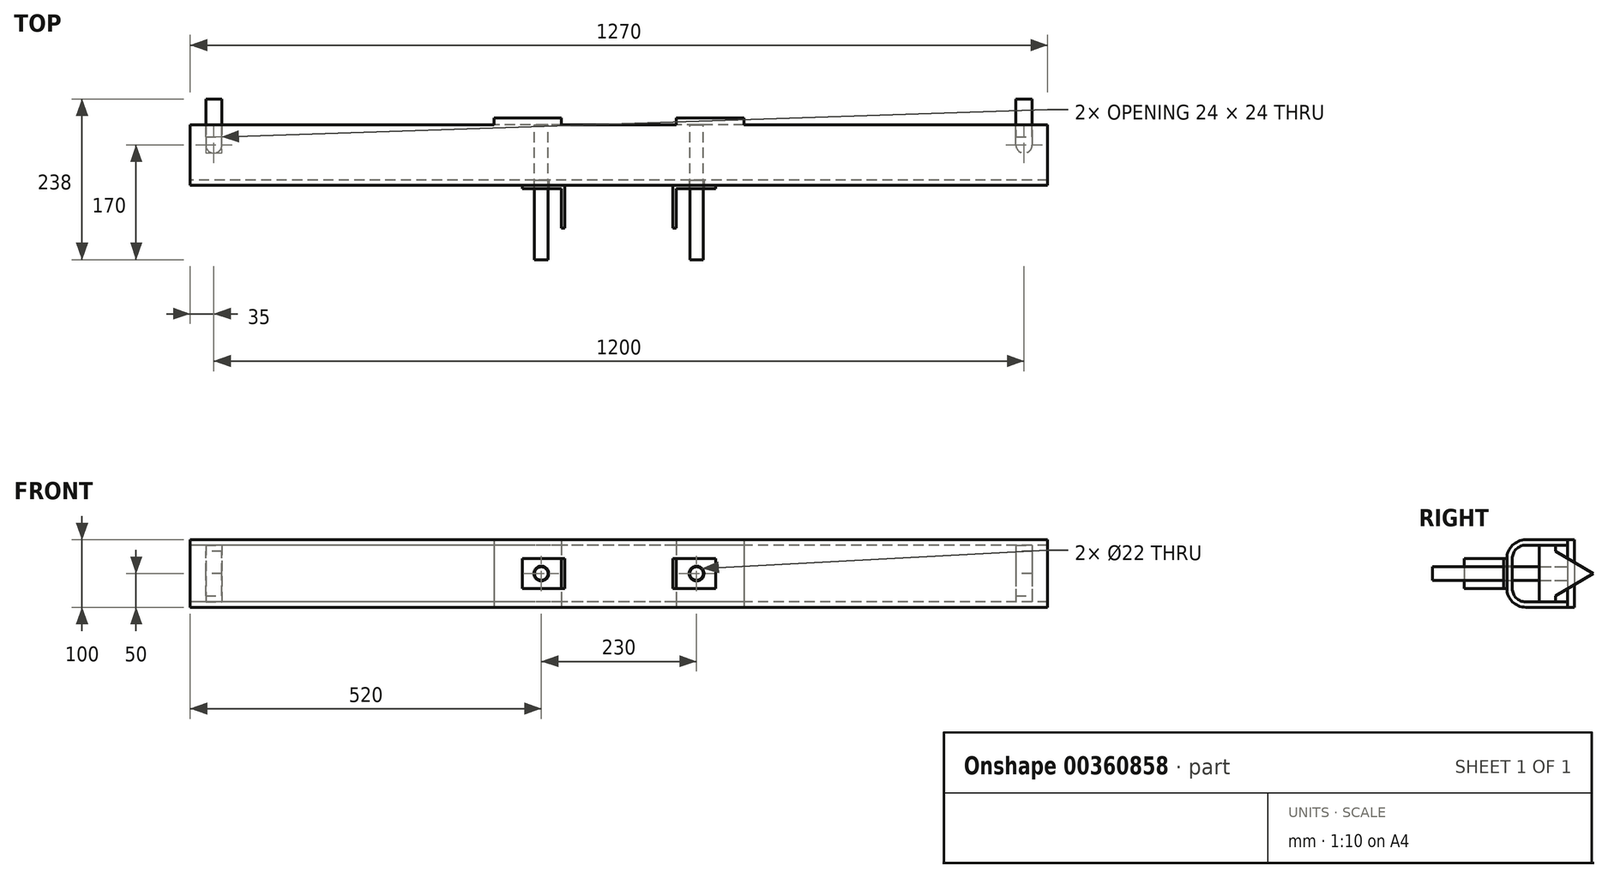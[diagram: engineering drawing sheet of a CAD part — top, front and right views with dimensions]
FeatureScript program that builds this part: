
annotation { "Feature Type Name" : "Feature", "Feature Type Description" : "" }
export const myFeature = defineFeature(function(context is Context, id is Id, definition is map)
    precondition{}
    {
        {
            var Q0;
            Q0=qCreatedBy(makeId("Right.planeOp"),FACE);
            var sketch = newSketch(context, id + "F0", { "sketchPlane" : qUnion([Q0])});
            skLineSegment(sketch, "E0", {"start": v(90, 50) * mm, "end": v(28, 50) * mm});
            skLineSegment(sketch, "E1", {"start": v(0, 22) * mm, "end": v(0, -22) * mm});
            skLineSegment(sketch, "E2", {"start": v(28, -50) * mm, "end": v(90, -50) * mm});
            skLineSegment(sketch, "E3", {"start": v(90, -50) * mm, "end": v(90, -42) * mm});
            skLineSegment(sketch, "E4", {"start": v(90, -42) * mm, "end": v(28, -42) * mm});
            skLineSegment(sketch, "E5", {"start": v(8, -22) * mm, "end": v(8, 22) * mm});
            skLineSegment(sketch, "E6", {"start": v(28, 42) * mm, "end": v(90, 42) * mm});
            skLineSegment(sketch, "E7", {"start": v(90, 42) * mm, "end": v(90, 50) * mm});
            skPoint(sketch, "E8.visualSharp", {"position": v(8, 42) * mm});
            skArc(sketch, "E8.filletArc", {"start": v(28, 42) * mm, "mid": v(13.86, 36.14) * mm, "end": v(8, 22) * mm});
            skPoint(sketch, "E9.visualSharp", {"position": v(8, -42) * mm});
            skArc(sketch, "E9.filletArc", {"start": v(8, -22) * mm, "mid": v(13.86, -36.14) * mm, "end": v(28, -42) * mm});
            skPoint(sketch, "E10.visualSharp", {"position": v(0, 50) * mm});
            skArc(sketch, "E10.filletArc", {"start": v(28, 50) * mm, "mid": v(8.2, 41.8) * mm, "end": v(0, 22) * mm});
            skPoint(sketch, "E11.visualSharp", {"position": v(0, -50) * mm});
            skArc(sketch, "E11.filletArc", {"start": v(0, -22) * mm, "mid": v(8.2, -41.8) * mm, "end": v(28, -50) * mm});
            skSolve(sketch);
        }
        {
            var Q0;
            Q0=qSketchRegion(id+"F0",true);
            extrude(context, id + "F1", {"entities" : qUnion([Q0]), "endBound" : BoundingType.SYMMETRIC, "depth" : 1270 * mm});
        }
        {
            var Q0;
            Q0=qCreatedBy(makeId("Top.planeOp"),FACE);
            var sketch = newSketch(context, id + "F2", { "sketchPlane" : qUnion([Q0])});
            skLineSegment(sketch, "E12", {"start": v(-143, 0) * mm, "end": v(-80, 0) * mm});
            skLineSegment(sketch, "E13", {"start": v(-80, 0) * mm, "end": v(-80, -63) * mm});
            skLineSegment(sketch, "E14.0", {"start": v(-85, -5) * mm, "end": v(-85, -63) * mm});
            skLineSegment(sketch, "E14.1", {"start": v(-143, -5) * mm, "end": v(-85, -5) * mm});
            skLineSegment(sketch, "E15", {"start": v(-143, -5) * mm, "end": v(-143, 0) * mm});
            skLineSegment(sketch, "E16", {"start": v(-85, -63) * mm, "end": v(-80, -63) * mm});
            skLineSegment(sketch, "E17.MirrorCS", {"start": v(85, -63) * mm, "end": v(80, -63) * mm});
            skLineSegment(sketch, "E18.MirrorCS", {"start": v(143, -5) * mm, "end": v(143, 0) * mm});
            skLineSegment(sketch, "E19.MirrorCS", {"start": v(143, 0) * mm, "end": v(80, 0) * mm});
            skLineSegment(sketch, "E20.MirrorCS", {"start": v(80, 0) * mm, "end": v(80, -63) * mm});
            skLineSegment(sketch, "E21.MirrorCS", {"start": v(143, -5) * mm, "end": v(85, -5) * mm});
            skLineSegment(sketch, "E22.MirrorCS", {"start": v(85, -5) * mm, "end": v(85, -63) * mm});
            skSolve(sketch);
        }
        {
            var Q0;
            Q0=qSketchRegion(id+"F2",true);
            extrude(context, id + "F3", {"entities" : qUnion([Q0]), "operationType" : NewBodyOperationType.ADD, "endBound" : BoundingType.SYMMETRIC, "depth" : 44 * mm});
        }
        {
            var Q0;
            Q0=makeQuery(id+"F1.opExtrude","SWEPT_FACE",FACE,{"disambiguationData":[OSD([sQuery(id+"F0.wireOp",EDGE,"E7")])]});
            var sketch = newSketch(context, id + "F4", { "sketchPlane" : qUnion([Q0])});
            skLineSegment(sketch, "E23.bottom", {"start": v(-185, 50) * mm, "end": v(-85, 50) * mm});
            skLineSegment(sketch, "E23.top", {"start": v(-185, -50) * mm, "end": v(-85, -50) * mm});
            skLineSegment(sketch, "E23.left", {"start": v(-185, 50) * mm, "end": v(-185, -50) * mm});
            skLineSegment(sketch, "E23.right", {"start": v(-85, 50) * mm, "end": v(-85, -50) * mm});
            skLineSegment(sketch, "E24.MirrorCS", {"start": v(85, 50) * mm, "end": v(85, -50) * mm});
            skLineSegment(sketch, "E25.MirrorCS", {"start": v(185, 50) * mm, "end": v(185, -50) * mm});
            skLineSegment(sketch, "E26.MirrorCS", {"start": v(185, 50) * mm, "end": v(85, 50) * mm});
            skLineSegment(sketch, "E27.MirrorCS", {"start": v(185, -50) * mm, "end": v(85, -50) * mm});
            skSolve(sketch);
        }
        {
            var Q0;
            Q0=qSketchRegion(id+"F4",true);
            extrude(context, id + "F5", {"entities" : qUnion([Q0]), "operationType" : NewBodyOperationType.ADD, "depth" : 10 * mm});
        }
        {
            var Q0;
            Q0=qCreatedBy(makeId("Front.planeOp"),FACE);
            var sketch = newSketch(context, id + "F6", { "sketchPlane" : qUnion([Q0])});
            skCircle(sketch, "E28", {"center": v(-115, 0) * mm, "radius": 11 * mm});
            skCircle(sketch, "E29.MirrorC", {"center": v(115, 0) * mm, "radius": 11 * mm});
            skSolve(sketch);
        }
        {
            var Q0;
            Q0=qSketchRegion(id+"F6",true);
            extrude(context, id + "F7", {"entities" : qUnion([Q0]), "operationType" : NewBodyOperationType.REMOVE, "endBound" : BoundingType.UP_TO_NEXT, "oppositeDirection" : true, "depth" : 25 * mm, "hasSecondDirection" : true, "secondDirectionBound" : SecondDirectionBoundingType.THROUGH_ALL, "secondDirectionOppositeDirection" : false, "secondDirectionDepth" : 25 * mm});
        }
        {
            var Q0;
            Q0=qCreatedBy(makeId("Top.planeOp"),FACE);
            var sketch = newSketch(context, id + "F8", { "sketchPlane" : qUnion([Q0])});
            skArc(sketch, "E30", {"start": v(-612, 60) * mm, "mid": v(-600, 48) * mm, "end": v(-588, 60) * mm});
            skArc(sketch, "E31.MirrorC", {"start": v(612, 60) * mm, "mid": v(600, 48) * mm, "end": v(588, 60) * mm});
            skLineSegment(sketch, "E32", {"start": v(-612, 60) * mm, "end": v(-612, 72) * mm});
            skLineSegment(sketch, "E33", {"start": v(-612, 72) * mm, "end": v(-588, 72) * mm});
            skLineSegment(sketch, "E34", {"start": v(-588, 72) * mm, "end": v(-588, 60) * mm});
            skLineSegment(sketch, "E35.MirrorCS", {"start": v(588, 72) * mm, "end": v(588, 60) * mm});
            skLineSegment(sketch, "E36.MirrorCS", {"start": v(612, 60) * mm, "end": v(612, 72) * mm});
            skLineSegment(sketch, "E37.MirrorCS", {"start": v(612, 72) * mm, "end": v(588, 72) * mm});
            skSolve(sketch);
        }
        {
            var Q0;
            Q0=qSketchRegion(id+"F8",true);
            var Q1;
            Q1=makeQuery(id+"F5.boolean.opBoolean","MERGE",FACE,{"derivedFrom":[makeQuery(id+"F1.opExtrude","SWEPT_FACE",FACE,{"disambiguationData":[OSD([sQuery(id+"F0.wireOp",EDGE,"E2")])]}),makeQuery(id+"F5.opExtrude","SWEPT_FACE",FACE,{"disambiguationData":[OSD([sQuery(id+"F4.wireOp",EDGE,"E23.top")])]}),makeQuery(id+"F5.opExtrude","SWEPT_FACE",FACE,{"disambiguationData":[OSD([sQuery(id+"F4.wireOp",EDGE,"E27.MirrorCS")])]})]});
            extrude(context, id + "F9", {"entities" : qUnion([Q0]), "operationType" : NewBodyOperationType.ADD, "endBoundEntityFace" : qUnion([Q1]), "depth" : 50 * mm, "hasSecondDirection" : true, "secondDirectionOppositeDirection" : true, "secondDirectionDepth" : 50 * mm});
        }
        {
            var Q0;
            Q0=makeQuery(id+"F5.opExtrude","CAP_FACE",FACE,{"disambiguationData":[OSD([sQuery(id+"F4.wireOp",EDGE,"E24.MirrorCS"),sQuery(id+"F4.wireOp",EDGE,"E25.MirrorCS"),sQuery(id+"F4.wireOp",EDGE,"E26.MirrorCS"),sQuery(id+"F4.wireOp",EDGE,"E27.MirrorCS")])],"isStart":true});
            var sketch = newSketch(context, id + "F10", { "sketchPlane" : qUnion([Q0])});
            skCircle(sketch, "E38", {"center": v(-115, 0) * mm, "radius": 10 * mm});
            skCircle(sketch, "E39.MirrorC", {"center": v(115, 0) * mm, "radius": 10 * mm});
            skSolve(sketch);
        }
        {
            var Q0;
            Q0=qSketchRegion(id+"F10",true);
            extrude(context, id + "F11", {"entities" : qUnion([Q0]), "operationType" : NewBodyOperationType.ADD, "depth" : 200 * mm});
        }
        {
            var Q0;
            Q0=qCreatedBy(makeId("Right.planeOp"),FACE);
            cPlane(context, id + "F12", {"entities" : qUnion([Q0]), "cplaneType" : CPlaneType.OFFSET, "offset" : 600 * mm, "width" : 150 * mm, "height" : 150 * mm});
        }
        {
            var Q0;
            Q0=qCreatedBy(id+"F12.planeOp",FACE);
            var sketch = newSketch(context, id + "F13", { "sketchPlane" : qUnion([Q0])});
            skLineSegment(sketch, "E40", {"start": v(60, -40) * mm, "end": v(60, 40) * mm});
            skLineSegment(sketch, "E41", {"start": v(60, 40) * mm, "end": v(128, 0) * mm});
            skLineSegment(sketch, "E42", {"start": v(128, 0) * mm, "end": v(60, -40) * mm});
            skLineSegment(sketch, "E43", {"start": v(0, 0) * mm, "end": v(156.79, 0) * mm, "construction": true});
            skSolve(sketch);
        }
        {
            var Q0;
            Q0 = qSketchRegion(id + "F13", true);
            extrude(context, id + "F14", {"entities" : qUnion([Q0]), "operationType" : NewBodyOperationType.ADD, "depth" : 12 * mm, "hasSecondDirection" : true, "secondDirectionOppositeDirection" : true, "secondDirectionDepth" : 12 * mm});
        }
        {
            var Q0;
            Q0=qCreatedBy(makeId("Right.planeOp"),FACE);
            cPlane(context, id + "F15", {"entities" : qUnion([Q0]), "cplaneType" : CPlaneType.OFFSET, "offset" : 600 * mm, "oppositeDirection" : true, "width" : 150 * mm, "height" : 150 * mm});
        }
        {
            var Q0;
            Q0=qCreatedBy(id+"F15.planeOp",FACE);
            var sketch = newSketch(context, id + "F16", { "sketchPlane" : qUnion([Q0])});
            skLineSegment(sketch, "E44", {"start": v(128, 0) * mm, "end": v(60, 40) * mm});
            skLineSegment(sketch, "E45", {"start": v(60, 40) * mm, "end": v(60, -40) * mm});
            skLineSegment(sketch, "E46", {"start": v(60, -40) * mm, "end": v(128, 0) * mm});
            skSolve(sketch);
        }
        {
            var Q0;
            Q0 = qSketchRegion(id + "F16", true);
            extrude(context, id + "F17", {"entities" : qUnion([Q0]), "operationType" : NewBodyOperationType.ADD, "depth" : 12 * mm, "hasSecondDirection" : true, "secondDirectionOppositeDirection" : true, "secondDirectionDepth" : 12 * mm});
        }
    });
